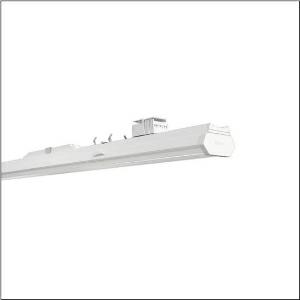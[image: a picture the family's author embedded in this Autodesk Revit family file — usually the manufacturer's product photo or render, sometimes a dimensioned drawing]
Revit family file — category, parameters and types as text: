
# Revit family: licross_r__21_protected_mo_52td12mn4a5g_9007
name_source: partatom
category: Lighting Fixtures
units: mm (PartAtom-declared; Revit-internal decimal feet)

## family parameters
Cut with Voids When Loaded = No
Host = Face
Light Source = No
Part Type = Normal
Room Calculation Point = No
Round Connector Dimension = Use Diameter
Shared = No

## types (1)
- --- (1 x LED, 10750 lm, 60.5 W, 4000K)
    Apparent Load = 61 VA
    CIE Flux Codes = 73 92 98 99 100
    Color Rendering = 80
    Color Temperature = 4000K
    Default Elevation = 1800 mm
    Description = Licross® 21 Protected MO, luminaire insert, of sheet steel, galvanised, coil coated, white, length: 1.500mm, width: 90mm, height: 101mm, LED rated luminous flux: 10.750lm, light colour: 840, control gear: ON/OFF Multilumen, with plug, 3-pole, with phase selection, mains connection: 220..240V, AC, 50/60Hz, rated input power: 61W, internal wiring halogen-free, primary light control with lens, of plastic, primary optical cover: cover, of PMMA, light emission: direct distribution, primary light characteristic: symmetric, protection rating (complete): IP54, insulation class (complete): insulation class I (protective earthing), certification: CE, ENEC, VDE, UKCA, protection symbol: D if used in an environment with non-conductive dust loads with corresponding accessories, impact resistance: IK06, permissible ambient temperature for indoor applications: -35..+45°C, corresponds to IFS (International Featured Standards) requirements for safety and quality in the food industry, reducing of maximum allowable ambient temperature of 5°C with ceiling mounting, LABS conformity tested according to VDMA 24364:2018-05, packaging unit: 1 piece
    Height = 92 mm
    Lamp = 1 x LED
    Lamp Light Flux = 10750 lm
    Lamp Power = 60.5 W
    Lamp count = 1
    Length = 1500 mm
    Luminous efficacy = 178 lm/W
    Manufacturer = Siteco
    ModVariant = No
    Model = 52TD12MN4A5G
    Mounting Place = Ceiling
    Mounting Type = Pendant
    Number of Poles = 1
    OnlyDefault = Yes
    Power Factor = 1
    Product Name = Licross® 21 Protected MO
    Product group = luminaire insert | ceiling pendant
    ProductGroupID = 902
    Protection Class = Protection class I
    Protection Degree = IP 54
    RLX_Detail_Level = 1
    RLX_Emergency_Light_Flux = 0 lm
    RLX_Emergency_Type = 0
    RLX_Emergency_Type_DB = No
    RlxData = <blob elided: 22185 chars, md5=7f1752a0>
    Socket = socket
    Standby Power = 0 W
    System Light Flux = 10750 lm
    System Power = 61 W
    Type Comments = factory setting: luminous flux: 100 % | (A | C | E) | 140 mA
    Type Image = l_1256148.jpg
    URL = http://relux.com
    VarID = @adj_130575
    Voltage = 0 V
    Weight = 0.00 kg
    Width = 88 mm

## geometry (parser evidence)
native form markers: Blend x4, Sweep x10
no freeform markers — native parametric forms only
